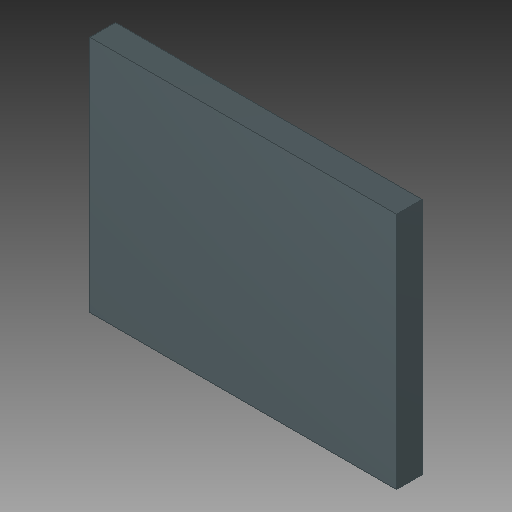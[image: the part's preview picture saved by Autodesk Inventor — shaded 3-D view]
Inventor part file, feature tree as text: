
AUTODESK INVENTOR PART (.ipt)
format: ipt  version: 2019.2 (Build 232265000, 265)  size: 91,136 bytes
history: native  units: mm
features: extrude x1, sketch x1
ambient origin geometry x8: Origin, YZ Plane, XZ Plane, XY Plane, X Axis, Y Axis, Z Axis, Center Point
bodies: Solid1 (feature_tree)
feature tree (2):
  extrude  "Extrusion1"  Depth=140.0mm
  sketch  "Sketch1"  dims[d0=180.0mm d1=140.0mm d2=15.0mm d3=0.0mm]
